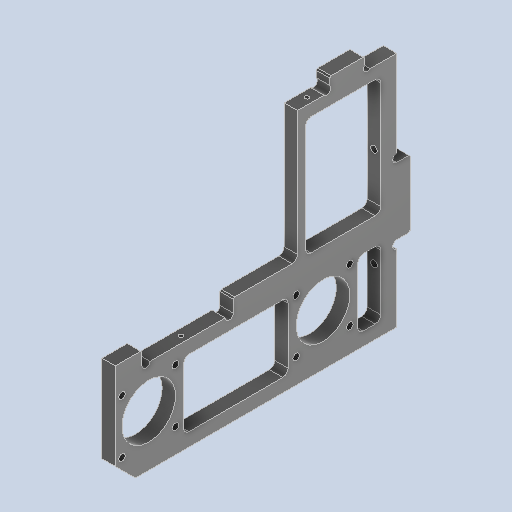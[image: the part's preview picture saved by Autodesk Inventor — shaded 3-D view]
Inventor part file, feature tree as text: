
AUTODESK INVENTOR PART (.ipt)
format: ipt  version: 2024.2 (Build 282272000, 272)  size: 390,144 bytes
history: native  units: mm
features: sketch x5, hole x3, chamfer x2, other x1, extrude x1
ambient origin geometry x8: Origin, YZ Plane, XZ Plane, XY Plane, X Axis, Y Axis, Z Axis, Center Point
bodies: Solid1 (feature_tree)
feature tree (12):
  other  "TorsoSideFrame.ipt"
  sketch  "Sketch2"  dims[d1=25.0mm d2=6.0mm d3=1.5mm d5=6.0mm d7=5.0mm d8=6.0mm d9=6.0mm d11=5.0mm d12=0.05mm d13=0.05mm d15=6.0mm d19=25.0mm]
  extrude  "Extrusion1"  Depth=25.0mm
  hole  "Side-M3"  [1 undecoded]
  hole  "Top-M3"  [1 undecoded]
  hole  "Top-M2"  [1 undecoded]
  chamfer  "C0.5"  Distance=2.0mm Angle=45.0deg
  chamfer  "C7.5"  [1 undecoded]
  sketch  "Sketch1"  dims[d0=10.0mm]
  sketch  "Sketch3"  dims[d20=15.0mm d21=35.0mm]
  sketch  "Sketch4"  dims[d22=5.0mm d23=34.0mm]
  sketch  "Sketch5"  dims[d24=37.0mm d25=5.0mm d26=0.0mm d27=2.459mm d28=6.0mm d29=4.0mm d30=2.0mm d31=90.0deg d32=8.0mm d33=20.594885mm d41=0.5mm d42=2.0mm d43=45.0deg d44=2.459mm d45=6.0mm d46=4.0mm d47=2.0mm d48=90.0deg d49=6.0mm d50=0.0mm d51=1.567mm d52=4.0mm d53=4.0mm d54=2.0mm d55=90.0deg d56=6.0mm d57=0.0mm d64=3.0mm d65=12.0mm d66=0.05mm d68=4.5mm d69=93.5mm d71=52.75mm d72=1.567mm d73=4.0mm d74=4.0mm d75=2.0mm d76=90.0deg d77=6.0mm d78=0.0mm d79=2.0mm d80=5.0mm d81=5.0mm d82=6.0mm d83=7.5mm d84=2.0mm d85=45.0deg]
note: 4 required parameter values undecoded (feature->parameter linkage not recoverable at this tier; creation-order binding heuristic only, values carry confidence <= 0.55)
